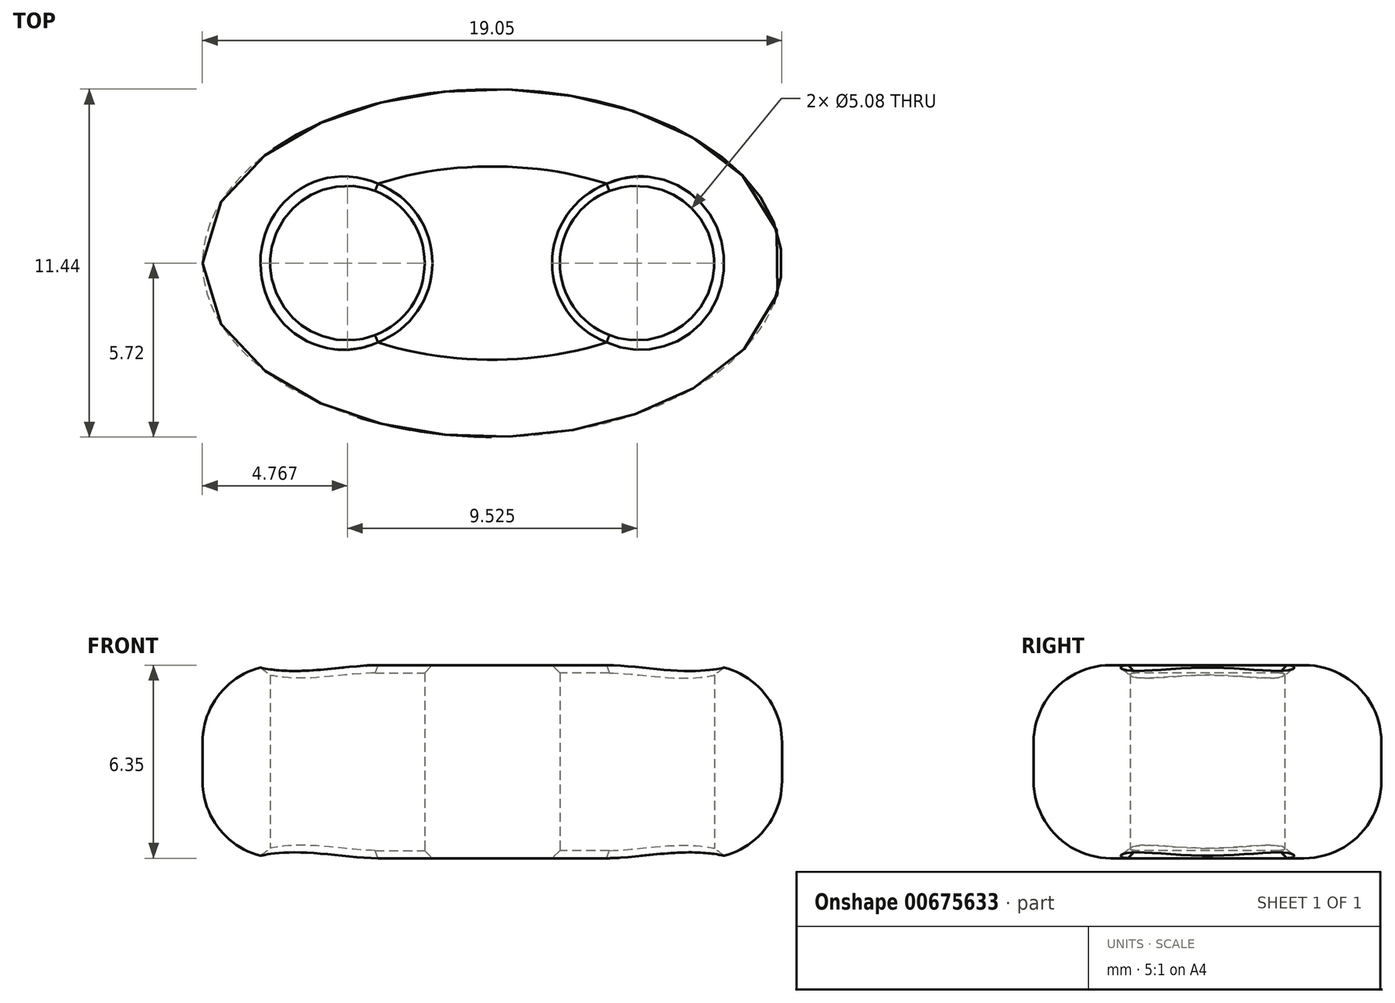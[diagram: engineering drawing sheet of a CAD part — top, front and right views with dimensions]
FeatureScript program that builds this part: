
annotation { "Feature Type Name" : "Feature", "Feature Type Description" : "" }
export const myFeature = defineFeature(function(context is Context, id is Id, definition is map)
    precondition{}
    {
        {
            var Q0;
            Q0=qCreatedBy(makeId("Top.planeOp"),FACE);
            var sketch = newSketch(context, id + "F0", { "sketchPlane" : qUnion([Q0])});
            skPoint(sketch, "E0.middle", {"position": v(0, 0) * mm});
            skCircle(sketch, "E1", {"center": v(-4.76, 0) * mm, "radius": 2.54 * mm});
            skCircle(sketch, "E2", {"center": v(4.76, 0) * mm, "radius": 2.54 * mm});
            skPoint(sketch, "E3", {"position": v(0, 5.72) * mm});
            skPoint(sketch, "E4", {"position": v(9.53, 0) * mm});
            skEllipse(sketch, "E5", {"center": v(0, 0) * mm, "majorRadius": 5.72 * mm, "minorRadius": 9.53 * mm, "majorAxis": v(0, 1)});
            skSolve(sketch);
        }
        {
            var Q0;
            Q0 = qSketchRegion(id + "F0", true);
            extrude(context, id + "F1", {"entities" : qUnion([Q0]), "depth" : 6.35 * mm, "offsetDistance" : 25.4 * mm});
        }
        {
            var Q0;
            Q0=makeQuery(id+"F1.opExtrude","CAP_EDGE",EDGE,{"disambiguationData":[OSD([sQuery(id+"F0.wireOp",EDGE,"E5")])],"isStart":false});
            var Q1;
            Q1=makeQuery(id+"F1.opExtrude","CAP_EDGE",EDGE,{"disambiguationData":[OSD([sQuery(id+"F0.wireOp",EDGE,"E5")])],"isStart":true});
            fillet(context, id + "F2", {"entities" : qUnion([Q0, Q1]), "radius" : 2.54 * mm, "tangentPropagation" : true, "allowEdgeOverflow" : false});
        }
        {
            var Q0;
            Q0=makeQuery(id+"F2.opFillet","BLEND_EDGE",EDGE,{"blendedFrom":[makeQuery(id+"F1.opExtrude","CAP_EDGE",EDGE,{"disambiguationData":[OSD([sQuery(id+"F0.wireOp",EDGE,"E5")])],"isStart":true}),makeQuery(id+"F1.opExtrude","SWEPT_FACE",FACE,{"disambiguationData":[OSD([sQuery(id+"F0.wireOp",EDGE,"E2")])]})],"blendedInto":[makeQuery(id+"F1.opExtrude","SWEPT_FACE",FACE,{"disambiguationData":[OSD([sQuery(id+"F0.wireOp",EDGE,"E2")])]})]});
            var Q1;
            Q1=makeQuery(id+"F1.opExtrude","CAP_EDGE",EDGE,{"disambiguationData":[OSD([sQuery(id+"F0.wireOp",EDGE,"E2")])],"isStart":true});
            var Q2;
            Q2=makeQuery(id+"F2.opFillet","BLEND_EDGE",EDGE,{"blendedFrom":[makeQuery(id+"F1.opExtrude","CAP_EDGE",EDGE,{"disambiguationData":[OSD([sQuery(id+"F0.wireOp",EDGE,"E5")])],"isStart":true}),makeQuery(id+"F1.opExtrude","SWEPT_FACE",FACE,{"disambiguationData":[OSD([sQuery(id+"F0.wireOp",EDGE,"E1")])]})],"blendedInto":[makeQuery(id+"F1.opExtrude","SWEPT_FACE",FACE,{"disambiguationData":[OSD([sQuery(id+"F0.wireOp",EDGE,"E1")])]})]});
            var Q3;
            Q3=makeQuery(id+"F1.opExtrude","CAP_EDGE",EDGE,{"disambiguationData":[OSD([sQuery(id+"F0.wireOp",EDGE,"E1")])],"isStart":true});
            var Q4;
            Q4=makeQuery(id+"F2.opFillet","BLEND_EDGE",EDGE,{"blendedFrom":[makeQuery(id+"F1.opExtrude","CAP_EDGE",EDGE,{"disambiguationData":[OSD([sQuery(id+"F0.wireOp",EDGE,"E5")])],"isStart":false}),makeQuery(id+"F1.opExtrude","SWEPT_FACE",FACE,{"disambiguationData":[OSD([sQuery(id+"F0.wireOp",EDGE,"E1")])]})],"blendedInto":[makeQuery(id+"F1.opExtrude","SWEPT_FACE",FACE,{"disambiguationData":[OSD([sQuery(id+"F0.wireOp",EDGE,"E1")])]})]});
            var Q5;
            Q5=makeQuery(id+"F1.opExtrude","CAP_EDGE",EDGE,{"disambiguationData":[OSD([sQuery(id+"F0.wireOp",EDGE,"E1")])],"isStart":false});
            var Q6;
            Q6=makeQuery(id+"F2.opFillet","BLEND_EDGE",EDGE,{"blendedFrom":[makeQuery(id+"F1.opExtrude","CAP_EDGE",EDGE,{"disambiguationData":[OSD([sQuery(id+"F0.wireOp",EDGE,"E5")])],"isStart":false}),makeQuery(id+"F1.opExtrude","SWEPT_FACE",FACE,{"disambiguationData":[OSD([sQuery(id+"F0.wireOp",EDGE,"E2")])]})],"blendedInto":[makeQuery(id+"F1.opExtrude","SWEPT_FACE",FACE,{"disambiguationData":[OSD([sQuery(id+"F0.wireOp",EDGE,"E2")])]})]});
            var Q7;
            Q7=makeQuery(id+"F1.opExtrude","CAP_EDGE",EDGE,{"disambiguationData":[OSD([sQuery(id+"F0.wireOp",EDGE,"E2")])],"isStart":false});
            chamfer(context, id + "F3", {"entities" : qUnion([Q0, Q1, Q2, Q3, Q4, Q5, Q6, Q7]), "width" : 0.25 * mm, "tangentPropagation" : true});
        }
    });
